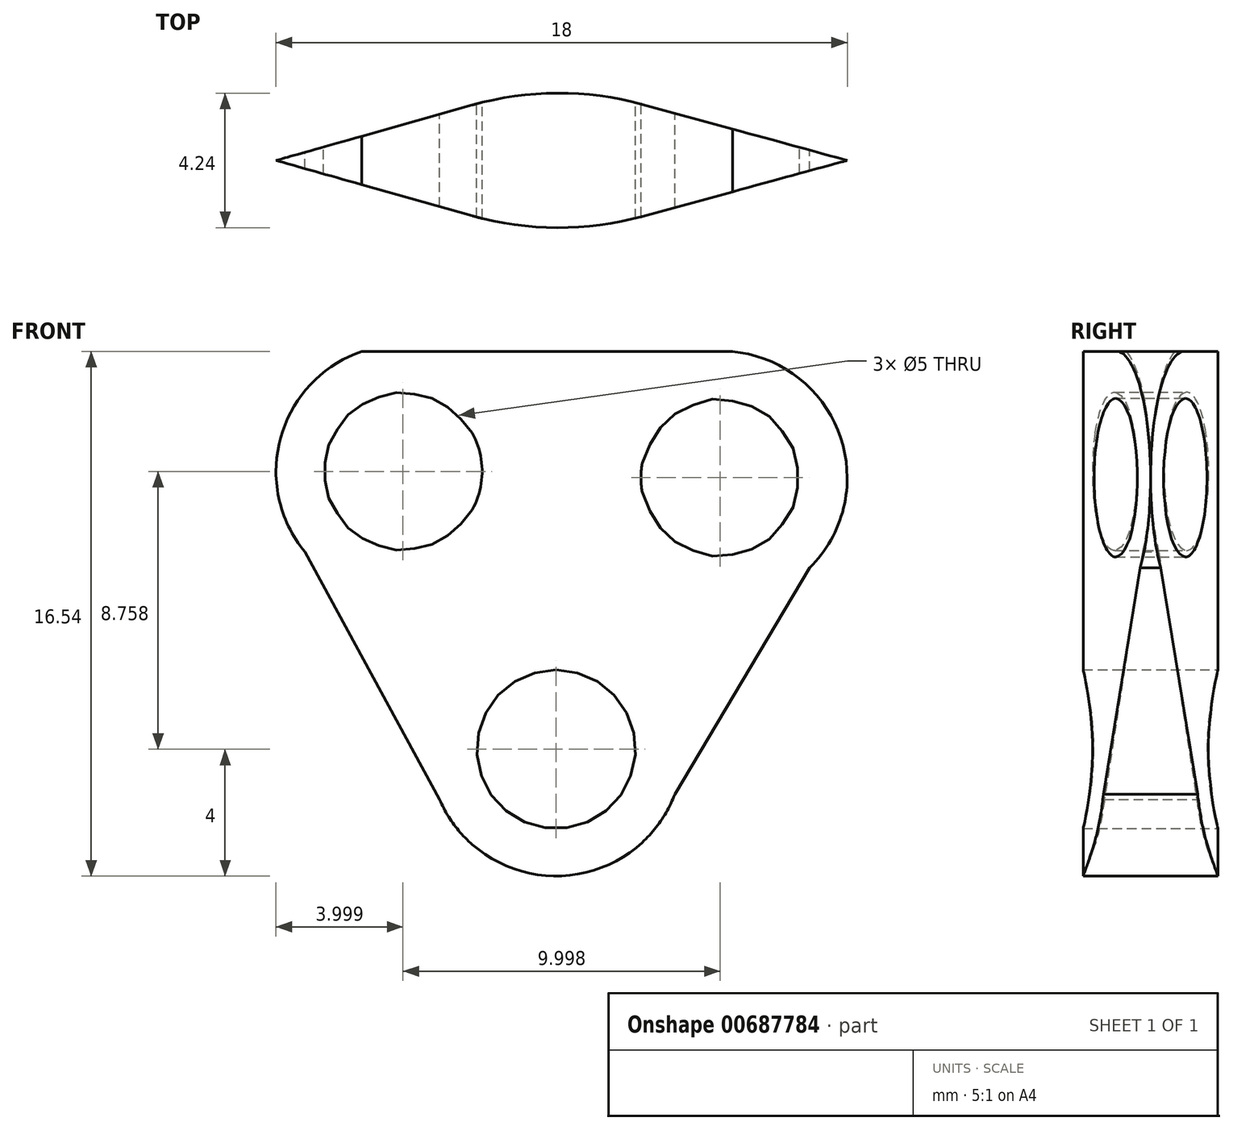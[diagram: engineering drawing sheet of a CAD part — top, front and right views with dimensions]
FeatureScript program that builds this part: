
annotation { "Feature Type Name" : "Feature", "Feature Type Description" : "" }
export const myFeature = defineFeature(function(context is Context, id is Id, definition is map)
    precondition{}
    {
        {
            var Q0;
            Q0=qCreatedBy(makeId("Front.planeOp"),FACE);
            var sketch = newSketch(context, id + "F0", { "sketchPlane" : qUnion([Q0])});
            skCircle(sketch, "E0", {"center": v(-22.81, 8.72) * mm, "radius": 2.5 * mm});
            skCircle(sketch, "E1", {"center": v(-12.81, 8.52) * mm, "radius": 2.5 * mm});
            skCircle(sketch, "E2", {"center": v(-22.81, 8.72) * mm, "radius": 4 * mm});
            skCircle(sketch, "E3.1.0.0", {"center": v(-12.81, 8.52) * mm, "radius": 4 * mm});
            skLineSegment(sketch, "E4", {"start": v(-22.67, 12.72) * mm, "end": v(-12.73, 12.52) * mm});
            skPoint(sketch, "E5", {"position": v(-17.99, -0.04) * mm});
            skCircle(sketch, "E6", {"center": v(-17.99, -0.04) * mm, "radius": 2.5 * mm});
            skCircle(sketch, "E7", {"center": v(-17.99, -0.04) * mm, "radius": 4 * mm});
            skLineSegment(sketch, "E8", {"start": v(-25.9, 6.18) * mm, "end": v(-21.66, -1.63) * mm});
            skLineSegment(sketch, "E9", {"start": v(-10, 5.68) * mm, "end": v(-14.25, -1.46) * mm});
            skSolve(sketch);
        }
        {
            var Q0;
            Q0=makeQuery(id+"F0.imprint","IMPRINT",FACE,{"disambiguationData":[TD([[makeQuery(id+"F0.imprint","IMPRINT",EDGE,{"derivedFrom":sQuery(id+"F0.wireOp",EDGE,"E6")}),-1.0]])]});
            var Q1;
            Q1=makeQuery(id+"F0.imprint","IMPRINT",FACE,{"disambiguationData":[TD([[makeQuery(id+"F0.imprint","IMPRINT",EDGE,{"derivedFrom":sQuery(id+"F0.wireOp",EDGE,"E1")}),-1.0]])]});
            var Q2;
            Q2=makeQuery(id+"F0.imprint","IMPRINT",FACE,{"disambiguationData":[TD([[makeQuery(id+"F0.imprint","IMPRINT",EDGE,{"derivedFrom":sQuery(id+"F0.wireOp",EDGE,"E6")}),1.0]])]});
            var Q3;
            Q3=makeQuery(id+"F0.imprint","IMPRINT",FACE,{"disambiguationData":[TD([[makeQuery(id+"F0.imprint","IMPRINT",EDGE,{"derivedFrom":sQuery(id+"F0.wireOp",EDGE,"E1")}),1.0]])]});
            var Q4;
            Q4=makeQuery(id+"F0.imprint","IMPRINT",FACE,{"disambiguationData":[TD([[makeQuery(id+"F0.imprint","IMPRINT",EDGE,{"derivedFrom":sQuery(id+"F0.wireOp",EDGE,"E0")}),1.0]])]});
            var Q5;
            {var subQ0=sQuery(id+"F0.wireOp",EDGE,"E4");Q5=makeQuery(id+"F0.imprint","IMPRINT",FACE,{"disambiguationData":[TD([[makeQuery(id+"F0.imprint","IMPRINT",EDGE,{"derivedFrom":subQ0}),-1.0]])]});}
            var Q6;
            Q6=makeQuery(id+"F0.imprint","IMPRINT",FACE,{"disambiguationData":[TD([[makeQuery(id+"F0.imprint","IMPRINT",EDGE,{"derivedFrom":sQuery(id+"F0.wireOp",EDGE,"E0")}),-1.0]])]});
            extrude(context, id + "F1", {"entities" : qUnion([Q0, Q1, Q2, Q3, Q4, Q5, Q6]), "depth" : 5 * mm, "offsetDistance" : 25 * mm});
        }
        {
            var Q0;
            Q0=makeQuery(id+"F0.imprint","IMPRINT",FACE,{"disambiguationData":[TD([[makeQuery(id+"F0.imprint","IMPRINT",EDGE,{"derivedFrom":sQuery(id+"F0.wireOp",EDGE,"E0")}),1.0]])]});
            var Q1;
            Q1=makeQuery(id+"F0.imprint","IMPRINT",FACE,{"disambiguationData":[TD([[makeQuery(id+"F0.imprint","IMPRINT",EDGE,{"derivedFrom":sQuery(id+"F0.wireOp",EDGE,"E1")}),1.0]])]});
            var Q2;
            Q2=makeQuery(id+"F0.imprint","IMPRINT",FACE,{"disambiguationData":[TD([[makeQuery(id+"F0.imprint","IMPRINT",EDGE,{"derivedFrom":sQuery(id+"F0.wireOp",EDGE,"E6")}),1.0]])]});
            extrude(context, id + "F2", {"entities" : qUnion([Q0, Q1, Q2]), "operationType" : NewBodyOperationType.REMOVE, "depth" : 7.6 * mm, "offsetDistance" : 25 * mm});
        }
        {
            var Q0;
            Q0=qCreatedBy(makeId("Top.planeOp"),FACE);
            var sketch = newSketch(context, id + "F3", { "sketchPlane" : qUnion([Q0])});
            skLineSegment(sketch, "E10", {"start": v(-20.63, -4.25) * mm, "end": v(-26.81, -2.5) * mm});
            skLineSegment(sketch, "E11", {"start": v(-15.27, -4.27) * mm, "end": v(-8.81, -2.5) * mm});
            skPoint(sketch, "E12.visualSharp", {"position": v(-17.95, -5) * mm});
            skArc(sketch, "E12.filletArc", {"start": v(-20.63, -4.25) * mm, "mid": v(-17.95, -4.62) * mm, "end": v(-15.27, -4.27) * mm});
            skArc(sketch, "E13.MirrorCS", {"start": v(-20.63, -0.75) * mm, "mid": v(-17.95, -0.38) * mm, "end": v(-15.27, -0.73) * mm});
            skLineSegment(sketch, "E14.MirrorCS", {"start": v(-20.63, -0.75) * mm, "end": v(-26.81, -2.5) * mm});
            skLineSegment(sketch, "E15.MirrorCS", {"start": v(-15.27, -0.73) * mm, "end": v(-8.81, -2.5) * mm});
            skPoint(sketch, "E16.orphan", {"position": v(-26.81, -5) * mm});
            skPoint(sketch, "E17.end.orphan", {"position": v(-26.81, 0) * mm});
            skPoint(sketch, "E18.orphan", {"position": v(-8.81, -5) * mm});
            skPoint(sketch, "E19.start.orphan", {"position": v(-8.81, 0) * mm});
            skPoint(sketch, "E20.0.0.start.orphan", {"position": v(-21.66, 0) * mm});
            skPoint(sketch, "E20.0.2.end.orphan", {"position": v(-21.66, -5) * mm});
            skPoint(sketch, "E21.trimOffspring.end.orphan", {"position": v(-14.25, -5) * mm});
            skPoint(sketch, "E20.0.1.start.orphan", {"position": v(-14.25, 0) * mm});
            skSolve(sketch);
        }
        {
            var Q0;
            Q0 = qSketchRegion(id + "F3", true);
            extrude(context, id + "F4", {"entities" : qUnion([Q0]), "operationType" : NewBodyOperationType.INTERSECT, "endBound" : BoundingType.SYMMETRIC, "depth" : 25 * mm, "offsetDistance" : 25 * mm});
        }
    });
